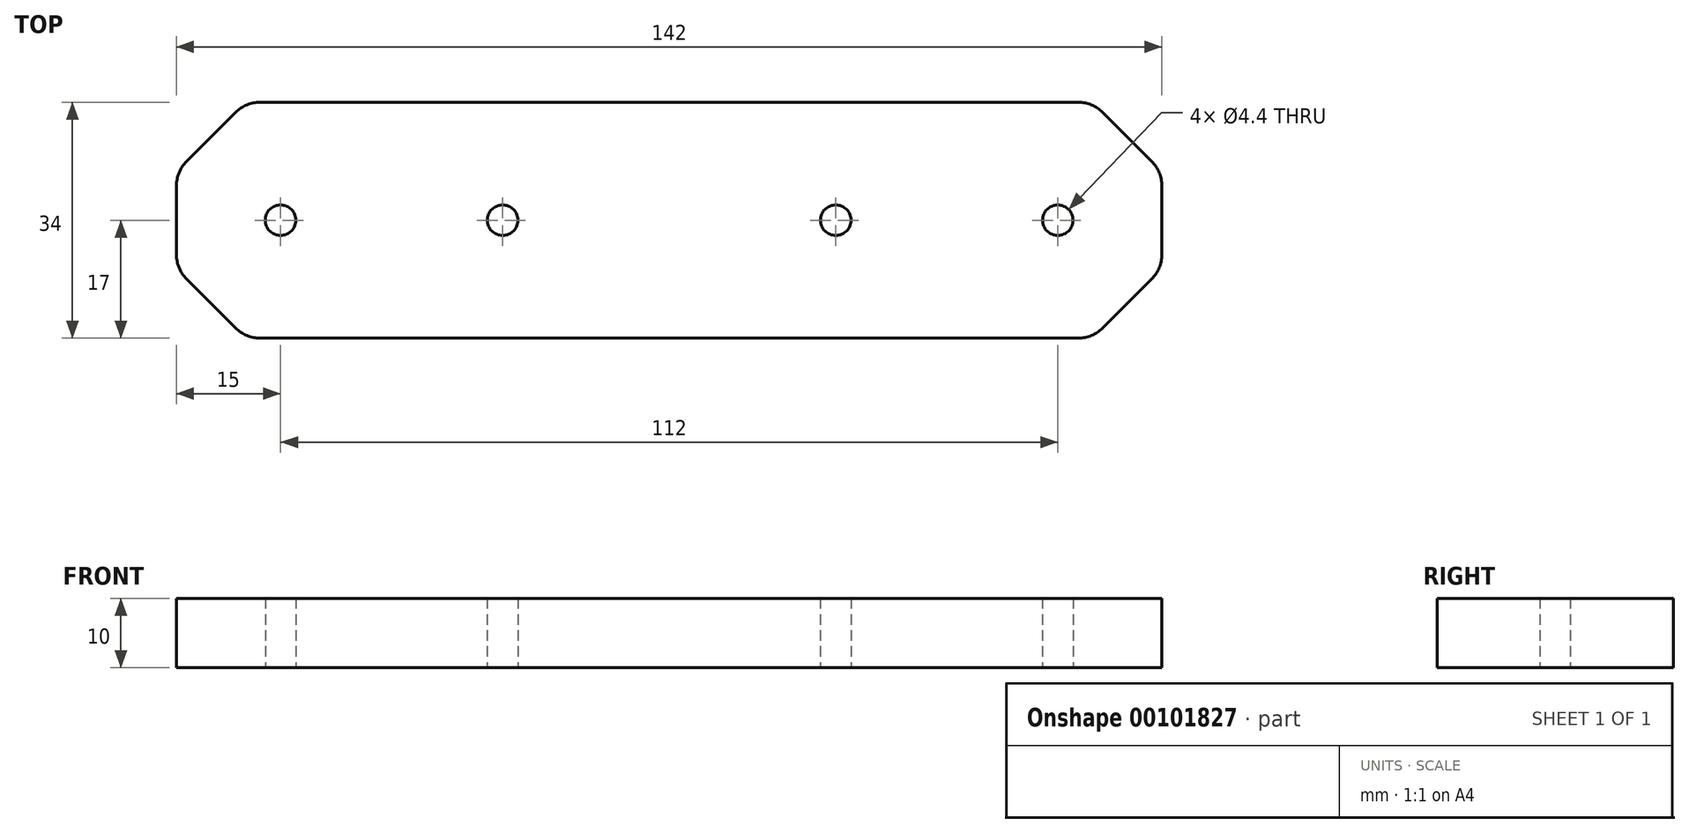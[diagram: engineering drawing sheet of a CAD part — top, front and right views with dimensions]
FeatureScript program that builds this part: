
annotation { "Feature Type Name" : "Feature", "Feature Type Description" : "" }
export const myFeature = defineFeature(function(context is Context, id is Id, definition is map)
    precondition{}
    {
        {
            var Q0;
            Q0=qCreatedBy(makeId("Top.planeOp"),FACE);
            var sketch = newSketch(context, id + "F0", { "sketchPlane" : qUnion([Q0])});
            skLineSegment(sketch, "E0.bottom", {"start": v(71, 17) * mm, "end": v(-71, 17) * mm});
            skLineSegment(sketch, "E0.top", {"start": v(71, -17) * mm, "end": v(-71, -17) * mm});
            skLineSegment(sketch, "E0.left", {"start": v(71, 17) * mm, "end": v(71, -17) * mm});
            skLineSegment(sketch, "E0.right", {"start": v(-71, 17) * mm, "end": v(-71, -17) * mm});
            skPoint(sketch, "E0.middle", {"position": v(0, 0) * mm});
            skSolve(sketch);
        }
        {
            var Q0;
            Q0 = qSketchRegion(id + "F0", true);
            extrude(context, id + "F1", {"entities" : qUnion([Q0]), "depth" : 10 * mm});
        }
        {
            var Q0;
            Q0=makeQuery(id+"F1.opExtrude","CAP_FACE",FACE,{"disambiguationData":[OSD([sQuery(id+"F0.wireOp",EDGE,"E0.bottom"),sQuery(id+"F0.wireOp",EDGE,"E0.top"),sQuery(id+"F0.wireOp",EDGE,"E0.left"),sQuery(id+"F0.wireOp",EDGE,"E0.right")])],"isStart":false});
            var sketch = newSketch(context, id + "F2", { "sketchPlane" : qUnion([Q0])});
            skPoint(sketch, "E1", {"position": v(-56, 0) * mm});
            skPoint(sketch, "E2", {"position": v(-24, 0) * mm});
            skPoint(sketch, "E3", {"position": v(24, 0) * mm});
            skPoint(sketch, "E4", {"position": v(56, 0) * mm});
            skSolve(sketch);
        }
        {
            var Q0;
            Q0=sQuery(id+"F2.wireOp",VERTEX,"E1");
            var Q1;
            Q1=sQuery(id+"F2.wireOp",VERTEX,"E2");
            var Q2;
            Q2=sQuery(id+"F2.wireOp",VERTEX,"E3");
            var Q3;
            Q3=sQuery(id+"F2.wireOp",VERTEX,"E4");
            var Q4;
            Q4=makeQuery(id+"F1.opExtrude","SWEPT_BODY",BODY,{"disambiguationData":[OSD([sQuery(id+"F0.wireOp",EDGE,"E0.bottom"),sQuery(id+"F0.wireOp",EDGE,"E0.top"),sQuery(id+"F0.wireOp",EDGE,"E0.left"),sQuery(id+"F0.wireOp",EDGE,"E0.right")])]});
            hole(context, id + "F3", {"style" : HoleStyle.SIMPLE, "endStyle" : HoleEndStyle.THROUGH, "standardTappedOrClearance" : lookupTablePath({ "standard" : "ISO", "fit" : "Normal", "size" : "M4", "type" : "Clearance" }), "standardBlindInLast" : lookupTablePath({ "fit" : "Standard", "standard" : "ISO", "size" : "M4", "type" : "Clearance" }), "holeDiameter" : 4.4 * mm, "locations" : qUnion([Q0, Q1, Q2, Q3]), "scope" : qUnion([Q4]), "isTappedThrough" : true});
        }
        {
            var Q0;
            Q0=makeQuery(id+"F1.opExtrude","SWEPT_EDGE",EDGE,{"disambiguationData":[OSD([sQuery(id+"F0.wireOp",EDGE,"E0.top"),sQuery(id+"F0.wireOp",EDGE,"E0.right")])]});
            var Q1;
            Q1=makeQuery(id+"F1.opExtrude","SWEPT_EDGE",EDGE,{"disambiguationData":[OSD([sQuery(id+"F0.wireOp",EDGE,"E0.top"),sQuery(id+"F0.wireOp",EDGE,"E0.left")])]});
            var Q2;
            Q2=makeQuery(id+"F1.opExtrude","SWEPT_EDGE",EDGE,{"disambiguationData":[OSD([sQuery(id+"F0.wireOp",EDGE,"E0.bottom"),sQuery(id+"F0.wireOp",EDGE,"E0.left")])]});
            var Q3;
            Q3=makeQuery(id+"F1.opExtrude","SWEPT_EDGE",EDGE,{"disambiguationData":[OSD([sQuery(id+"F0.wireOp",EDGE,"E0.bottom"),sQuery(id+"F0.wireOp",EDGE,"E0.right")])]});
            chamfer(context, id + "F4", {"entities" : qUnion([Q0, Q1, Q2, Q3]), "width" : 10 * mm, "tangentPropagation" : true});
        }
        {
            var Q0;
            {var subQ0=sQuery(id+"F0.wireOp",EDGE,"E0.top");Q0=makeQuery(id+"F4.opChamfer","BLEND_EDGE",EDGE,{"blendedFrom":[makeQuery(id+"F1.opExtrude","SWEPT_EDGE",EDGE,{"disambiguationData":[OSD([subQ0,sQuery(id+"F0.wireOp",EDGE,"E0.right")])]}),makeQuery(id+"F1.opExtrude","SWEPT_FACE",FACE,{"disambiguationData":[OSD([subQ0])]})],"blendedInto":[makeQuery(id+"F1.opExtrude","SWEPT_FACE",FACE,{"disambiguationData":[OSD([subQ0])]})]});}
            var Q1;
            {var subQ0=sQuery(id+"F0.wireOp",EDGE,"E0.right");Q1=makeQuery(id+"F4.opChamfer","BLEND_EDGE",EDGE,{"blendedFrom":[makeQuery(id+"F1.opExtrude","SWEPT_EDGE",EDGE,{"disambiguationData":[OSD([sQuery(id+"F0.wireOp",EDGE,"E0.top"),subQ0])]}),makeQuery(id+"F1.opExtrude","SWEPT_FACE",FACE,{"disambiguationData":[OSD([subQ0])]})],"blendedInto":[makeQuery(id+"F1.opExtrude","SWEPT_FACE",FACE,{"disambiguationData":[OSD([subQ0])]})]});}
            var Q2;
            {var subQ0=sQuery(id+"F0.wireOp",EDGE,"E0.top");Q2=makeQuery(id+"F4.opChamfer","BLEND_EDGE",EDGE,{"blendedFrom":[makeQuery(id+"F1.opExtrude","SWEPT_EDGE",EDGE,{"disambiguationData":[OSD([subQ0,sQuery(id+"F0.wireOp",EDGE,"E0.left")])]}),makeQuery(id+"F1.opExtrude","SWEPT_FACE",FACE,{"disambiguationData":[OSD([subQ0])]})],"blendedInto":[makeQuery(id+"F1.opExtrude","SWEPT_FACE",FACE,{"disambiguationData":[OSD([subQ0])]})]});}
            var Q3;
            {var subQ0=sQuery(id+"F0.wireOp",EDGE,"E0.left");Q3=makeQuery(id+"F4.opChamfer","BLEND_EDGE",EDGE,{"blendedFrom":[makeQuery(id+"F1.opExtrude","SWEPT_EDGE",EDGE,{"disambiguationData":[OSD([sQuery(id+"F0.wireOp",EDGE,"E0.top"),subQ0])]}),makeQuery(id+"F1.opExtrude","SWEPT_FACE",FACE,{"disambiguationData":[OSD([subQ0])]})],"blendedInto":[makeQuery(id+"F1.opExtrude","SWEPT_FACE",FACE,{"disambiguationData":[OSD([subQ0])]})]});}
            var Q4;
            {var subQ0=sQuery(id+"F0.wireOp",EDGE,"E0.left");Q4=makeQuery(id+"F4.opChamfer","BLEND_EDGE",EDGE,{"blendedFrom":[makeQuery(id+"F1.opExtrude","SWEPT_EDGE",EDGE,{"disambiguationData":[OSD([sQuery(id+"F0.wireOp",EDGE,"E0.bottom"),subQ0])]}),makeQuery(id+"F1.opExtrude","SWEPT_FACE",FACE,{"disambiguationData":[OSD([subQ0])]})],"blendedInto":[makeQuery(id+"F1.opExtrude","SWEPT_FACE",FACE,{"disambiguationData":[OSD([subQ0])]})]});}
            var Q5;
            {var subQ0=sQuery(id+"F0.wireOp",EDGE,"E0.bottom");Q5=makeQuery(id+"F4.opChamfer","BLEND_EDGE",EDGE,{"blendedFrom":[makeQuery(id+"F1.opExtrude","SWEPT_EDGE",EDGE,{"disambiguationData":[OSD([subQ0,sQuery(id+"F0.wireOp",EDGE,"E0.left")])]}),makeQuery(id+"F1.opExtrude","SWEPT_FACE",FACE,{"disambiguationData":[OSD([subQ0])]})],"blendedInto":[makeQuery(id+"F1.opExtrude","SWEPT_FACE",FACE,{"disambiguationData":[OSD([subQ0])]})]});}
            var Q6;
            {var subQ0=sQuery(id+"F0.wireOp",EDGE,"E0.bottom");Q6=makeQuery(id+"F4.opChamfer","BLEND_EDGE",EDGE,{"blendedFrom":[makeQuery(id+"F1.opExtrude","SWEPT_EDGE",EDGE,{"disambiguationData":[OSD([subQ0,sQuery(id+"F0.wireOp",EDGE,"E0.right")])]}),makeQuery(id+"F1.opExtrude","SWEPT_FACE",FACE,{"disambiguationData":[OSD([subQ0])]})],"blendedInto":[makeQuery(id+"F1.opExtrude","SWEPT_FACE",FACE,{"disambiguationData":[OSD([subQ0])]})]});}
            var Q7;
            {var subQ0=sQuery(id+"F0.wireOp",EDGE,"E0.right");Q7=makeQuery(id+"F4.opChamfer","BLEND_EDGE",EDGE,{"blendedFrom":[makeQuery(id+"F1.opExtrude","SWEPT_EDGE",EDGE,{"disambiguationData":[OSD([sQuery(id+"F0.wireOp",EDGE,"E0.bottom"),subQ0])]}),makeQuery(id+"F1.opExtrude","SWEPT_FACE",FACE,{"disambiguationData":[OSD([subQ0])]})],"blendedInto":[makeQuery(id+"F1.opExtrude","SWEPT_FACE",FACE,{"disambiguationData":[OSD([subQ0])]})]});}
            fillet(context, id + "F5", {"entities" : qUnion([Q0, Q1, Q2, Q3, Q4, Q5, Q6, Q7]), "radius" : 5 * mm, "tangentPropagation" : true, "allowEdgeOverflow" : false});
        }
    });
